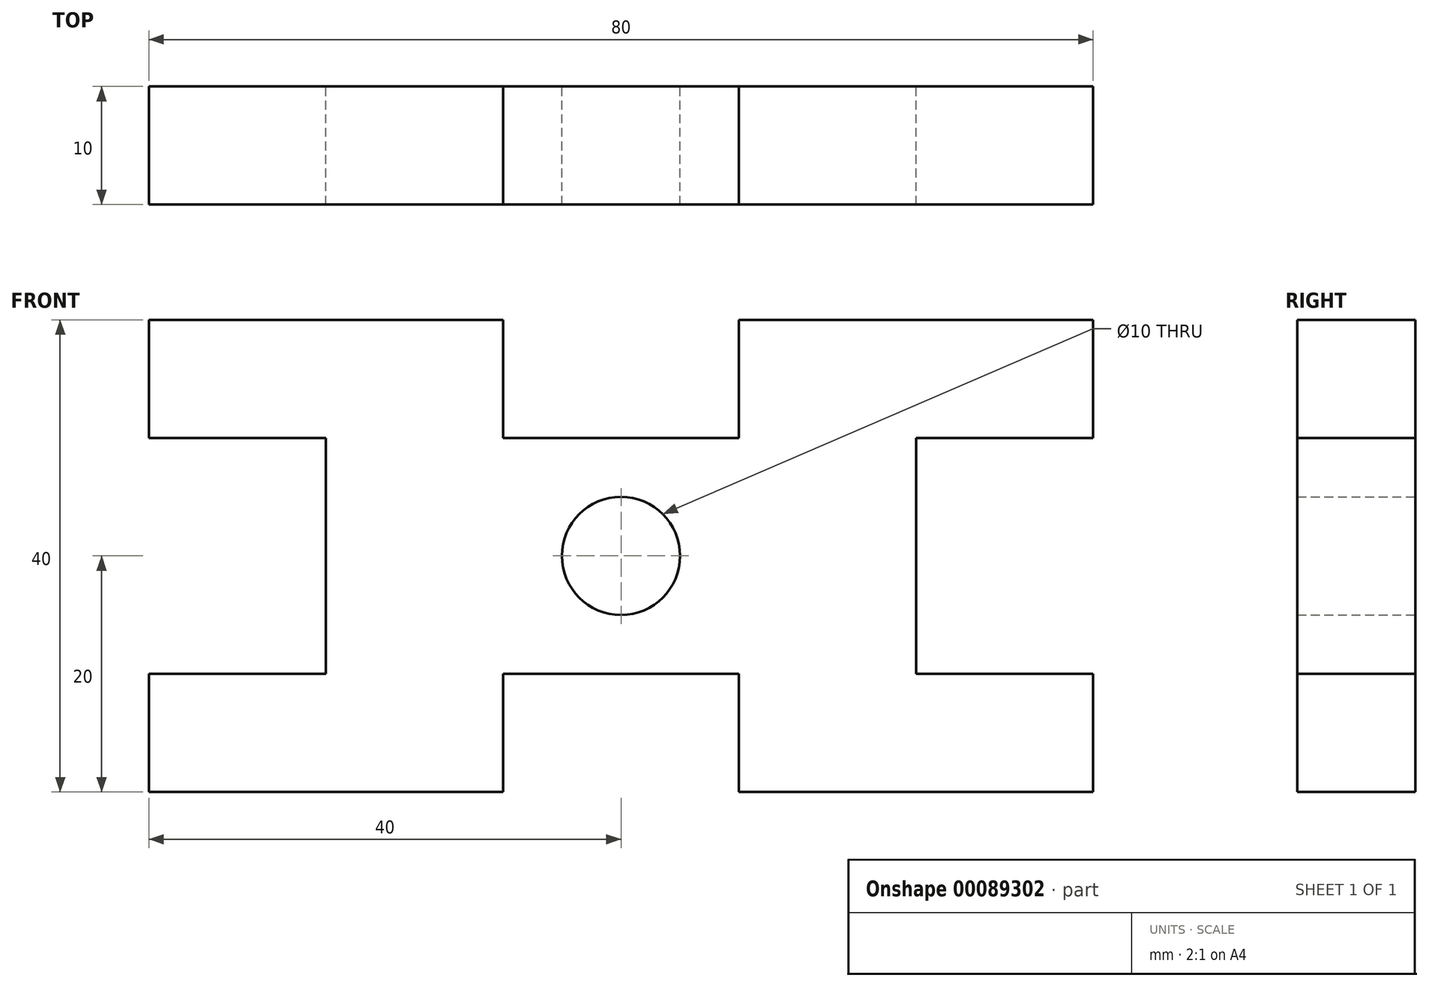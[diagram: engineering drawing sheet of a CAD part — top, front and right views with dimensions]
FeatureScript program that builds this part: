
annotation { "Feature Type Name" : "Feature", "Feature Type Description" : "" }
export const myFeature = defineFeature(function(context is Context, id is Id, definition is map)
    precondition{}
    {
        {
            var Q0;
            Q0=qCreatedBy(makeId("Front.planeOp"),FACE);
            var sketch = newSketch(context, id + "F0", { "sketchPlane" : qUnion([Q0])});
            skCircle(sketch, "E0", {"center": v(0, 0) * mm, "radius": 5 * mm});
            skLineSegment(sketch, "E1", {"start": v(0, -10) * mm, "end": v(-10, -10) * mm});
            skLineSegment(sketch, "E2", {"start": v(-10, -10) * mm, "end": v(-10, -20) * mm});
            skLineSegment(sketch, "E3", {"start": v(-10, -20) * mm, "end": v(-40, -20) * mm});
            skLineSegment(sketch, "E4", {"start": v(-40, -20) * mm, "end": v(-40, -10) * mm});
            skLineSegment(sketch, "E5", {"start": v(-40, -10) * mm, "end": v(-25, -10) * mm});
            skLineSegment(sketch, "E6", {"start": v(-25, -10) * mm, "end": v(-25, 10) * mm});
            skLineSegment(sketch, "E7", {"start": v(-25, 10) * mm, "end": v(-40, 10) * mm});
            skLineSegment(sketch, "E8", {"start": v(-40, 10) * mm, "end": v(-40, 20) * mm});
            skLineSegment(sketch, "E9", {"start": v(-40, 20) * mm, "end": v(-10, 20) * mm});
            skLineSegment(sketch, "E10", {"start": v(-10, 20) * mm, "end": v(-10, 10) * mm});
            skLineSegment(sketch, "E11", {"start": v(-10, 10) * mm, "end": v(0, 10) * mm});
            skLineSegment(sketch, "E12", {"start": v(0, 10) * mm, "end": v(0, -10) * mm, "construction": true});
            skLineSegment(sketch, "E13.MirrorCS", {"start": v(25, 10) * mm, "end": v(40, 10) * mm});
            skLineSegment(sketch, "E14.MirrorCS", {"start": v(10, -10) * mm, "end": v(10, -20) * mm});
            skLineSegment(sketch, "E15.MirrorCS", {"start": v(10, -20) * mm, "end": v(40, -20) * mm});
            skLineSegment(sketch, "E16.MirrorCS", {"start": v(0, -10) * mm, "end": v(10, -10) * mm});
            skLineSegment(sketch, "E17.MirrorCS", {"start": v(40, -20) * mm, "end": v(40, -10) * mm});
            skLineSegment(sketch, "E18.MirrorCS", {"start": v(40, -10) * mm, "end": v(25, -10) * mm});
            skLineSegment(sketch, "E19.MirrorCS", {"start": v(10, 10) * mm, "end": v(0, 10) * mm});
            skLineSegment(sketch, "E20.MirrorCS", {"start": v(10, 20) * mm, "end": v(10, 10) * mm});
            skLineSegment(sketch, "E21.MirrorCS", {"start": v(40, 20) * mm, "end": v(10, 20) * mm});
            skLineSegment(sketch, "E22.MirrorCS", {"start": v(40, 10) * mm, "end": v(40, 20) * mm});
            skLineSegment(sketch, "E23.MirrorCS", {"start": v(25, -10) * mm, "end": v(25, 10) * mm});
            skSolve(sketch);
        }
        {
            var Q0;
            Q0 = qSketchRegion(id + "F0", true);
            extrude(context, id + "F1", {"entities" : qUnion([Q0]), "depth" : 10 * mm});
        }
    });
